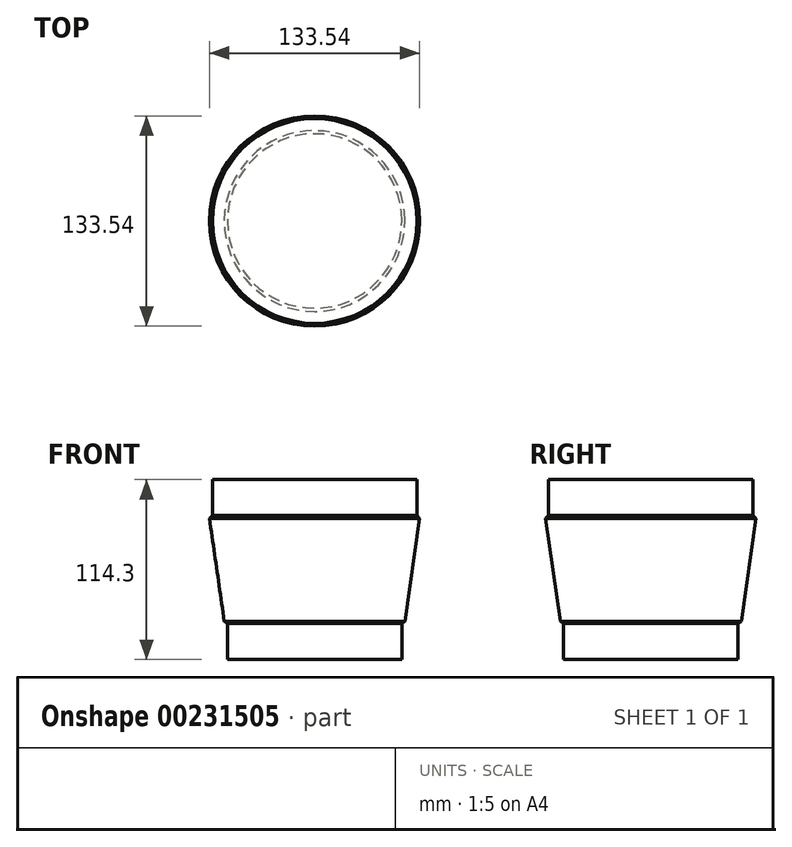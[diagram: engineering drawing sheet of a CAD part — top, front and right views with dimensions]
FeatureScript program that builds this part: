
annotation { "Feature Type Name" : "Feature", "Feature Type Description" : "" }
export const myFeature = defineFeature(function(context is Context, id is Id, definition is map)
    precondition{}
    {
        {
            var Q0;
            Q0=qCreatedBy(makeId("Front.planeOp"),FACE);
            var sketch = newSketch(context, id + "F0", { "sketchPlane" : qUnion([Q0])});
            skLineSegment(sketch, "E0", {"start": v(0, 0) * mm, "end": v(0, 50.43) * mm, "construction": true});
            skLineSegment(sketch, "E1", {"start": v(64.06, 114.3) * mm, "end": v(64.97, 114.3) * mm});
            skLineSegment(sketch, "E2", {"start": v(64.97, 114.3) * mm, "end": v(64.97, 91.44) * mm});
            skLineSegment(sketch, "E3", {"start": v(64.97, 91.44) * mm, "end": v(66.77, 89.64) * mm});
            skLineSegment(sketch, "E4", {"start": v(55.37, 22.86) * mm, "end": v(57.4, 24.38) * mm});
            skLineSegment(sketch, "E5", {"start": v(57.4, 24.38) * mm, "end": v(66.77, 89.64) * mm});
            skLineSegment(sketch, "E6", {"start": v(55.37, 22.86) * mm, "end": v(55.37, 0) * mm});
            skLineSegment(sketch, "E7", {"start": v(64.97, 114.3) * mm, "end": v(0, 114.3) * mm});
            skLineSegment(sketch, "E8", {"start": v(0, 114.3) * mm, "end": v(0, 0) * mm});
            skLineSegment(sketch, "E9", {"start": v(55.37, 0) * mm, "end": v(0, 0) * mm});
            skSolve(sketch);
        }
        {
            var Q0;
            Q0 = qSketchRegion(id + "F0", true);
            var Q1;
            Q1=sQuery(id+"F0.wireOp",EDGE,"E0");
            revolve(context, id + "F1", {"entities" : qUnion([Q0]), "axis" : qUnion([Q1]), "revolveType" : RevolveType.FULL});
        }
    });
